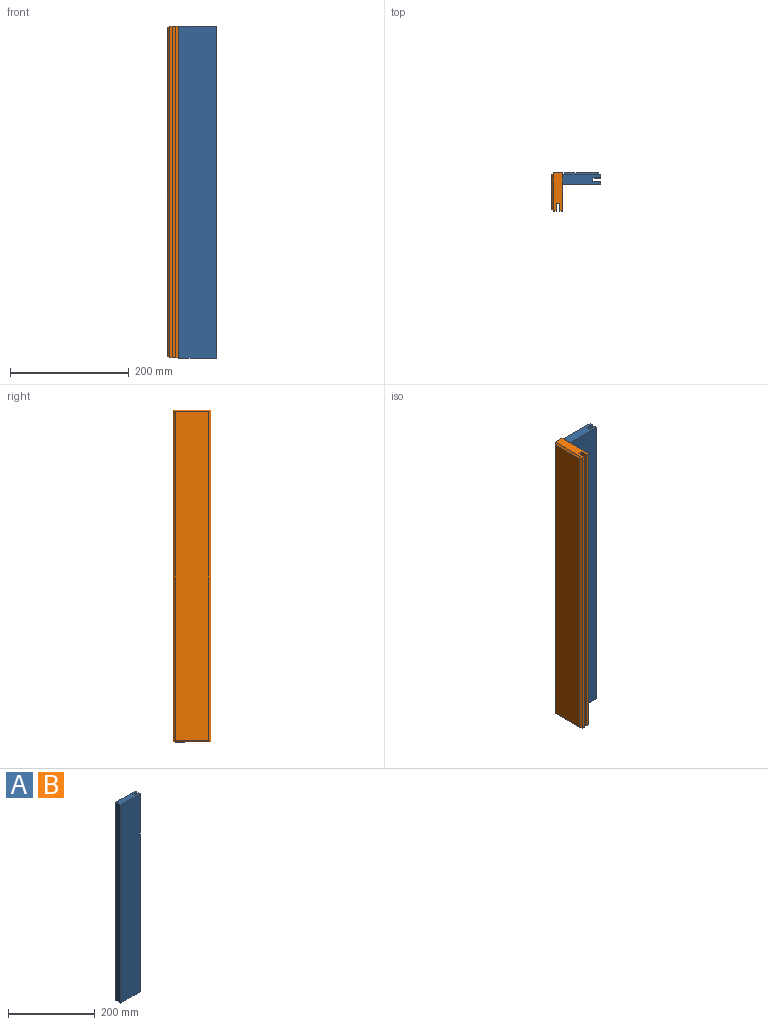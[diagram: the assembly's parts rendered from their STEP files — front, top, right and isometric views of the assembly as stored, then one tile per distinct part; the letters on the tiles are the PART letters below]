
ASSEMBLY  parts=2 mates=1
PART A: 14 faces, bbox 63.5x19.1x558.8 mm
  f0: plane 558.8x4.76mm, normal (1,0,0), area 2661.3mm2, adj f1,f4,f6,f13
  f1: plane 63.5x15.88mm, normal (0,0,-1), area 927.4mm2, adj f0,f3,f4,f5,f7,f11,f12,f13
  f2: plane 552.45x57.15mm, normal (0,1,0), area 31572.5mm2, adj f7,f8,f9,f10
  f3: plane 558.8x15.88mm, normal (-1,0,0), area 8870.9mm2, adj f1,f4,f6,f8
  f4: plane 558.8x63.5mm, normal (0,-1,0), area 35483.8mm2, adj f0,f1,f3,f6
  f5: plane 558.8x4.76mm, normal (1,0,0), area 2661.3mm2, adj f1,f6,f9,f12
  f6: plane 63.5x15.88mm, normal (0,0,1), area 927.4mm2, adj f0,f3,f4,f5,f10,f11,f12,f13
  f7: plane 63.5x3.18mm, normal (0,0.71,-0.71), area 270.9mm2, adj f1,f2,f8,f9
  f8: plane 558.8x3.18mm, normal (-0.71,0.71,0), area 2494.8mm2, adj f2,f3,f7,f10
  f9: plane 558.8x3.18mm, normal (0.71,0.71,0), area 2494.8mm2, adj f2,f5,f7,f10
  f10: plane 63.5x3.18mm, normal (0,0.71,0.71), area 270.9mm2, adj f2,f6,f8,f9
  f11: plane 558.8x6.35mm, normal (1,0,0), area 3548.4mm2, adj f1,f6,f12,f13
  f12: plane 558.8x12.7mm, normal (0,-1,0), area 7096.8mm2, adj f1,f5,f6,f11
  f13: plane 558.8x12.7mm, normal (0,1,0), area 7096.8mm2, adj f0,f1,f6,f11
PART B: same geometry as A
PLACE A t=(-203.01,95.93,-61.75)mm
PLACE B rot(axis=(0.71,-0.71,0),180deg) t=(-203.01,114.98,497.05)mm
MATE fastened B.f4 <-> A.f3  axis (1,0,0) through (-203.01,114.98,-61.75)mm
